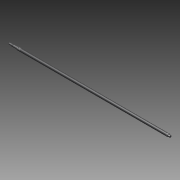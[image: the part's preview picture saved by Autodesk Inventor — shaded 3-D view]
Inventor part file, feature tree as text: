
AUTODESK INVENTOR PART (.ipt)
format: ipt  version: 2011 SP1 (Build 150282100, 282)  size: 123,904 bytes
history: native  units: mm
features: other x21, sketch x5, revolve x3, thread x2, extrude x2
ambient origin geometry x8: Origin, YZ Plane, XZ Plane, XY Plane, X Axis, Y Axis, Z Axis, Center Point
bodies: Solid1 (feature_tree)
feature tree (33):
  revolve  "Revolution1"  [1 undecoded]
  thread  "Thread1"  [1 undecoded]
  revolve  "Revolution2"  [1 undecoded]
  thread  "Thread2"  [1 undecoded]
  extrude  "Extrusion1"  TaperAngle=0.0deg  [1 undecoded]
  extrude  "Extrusion2"  [1 undecoded]
  revolve  "Revolution3"  [1 undecoded]
  other  "FSS_XY"
  other  "FSS_YZ"
  other  "FSS_ZX"
  other  "FSS_X"
  other  "FSS_Y"
  other  "FSS_Z"
  other  "FSS_Center"
  other  "SSS_XY"
  other  "SSS_YZ"
  other  "SSS_ZX"
  other  "SSS_X"
  other  "SSS_Y"
  other  "SSS_Z"
  other  "SSS_Center"
  other  "bnt_s_1_XY"
  other  "bnt_s_1_YZ"
  other  "bnt_s_1_ZX"
  other  "bnt_s_1_X"
  other  "bnt_s_1_Y"
  other  "bnt_s_1_Z"
  other  "bnt_s_1_Center"
  sketch  "Sketch_1"  dims[d0=360.0deg d1=1058.0mm d2=0.0mm d3=360.0deg]
  sketch  "Sketch_10"  dims[d4=11.3865mm d5=0.0mm d6=4.0mm d7=0.0mm d8=4.0mm d9=0.0mm]
  sketch  "Sketch_11"  dims[d10=360.0deg d11=0.0mm d12=0.0mm d13=0.0mm]
  sketch  "Sketch_12"
  sketch  "Sketch_16"
note: 7 required parameter values undecoded (feature->parameter linkage not recoverable at this tier; creation-order binding heuristic only, values carry confidence <= 0.55)